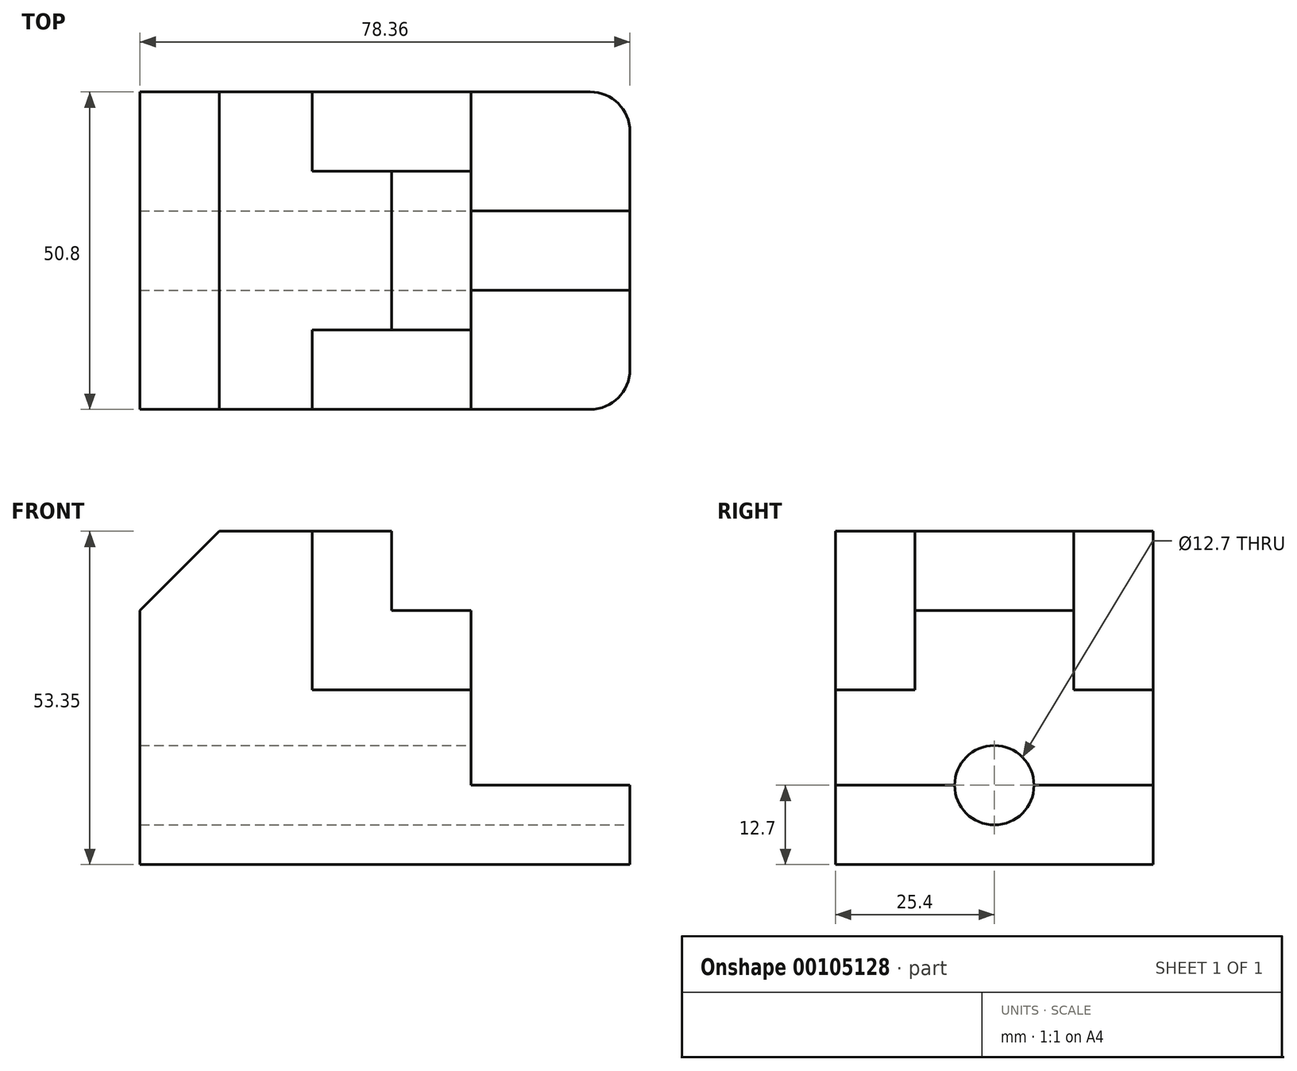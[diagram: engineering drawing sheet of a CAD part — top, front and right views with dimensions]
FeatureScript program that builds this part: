
annotation { "Feature Type Name" : "Feature", "Feature Type Description" : "" }
export const myFeature = defineFeature(function(context is Context, id is Id, definition is map)
    precondition{}
    {
        {
            var Q0;
            Q0=qCreatedBy(makeId("Front.planeOp"),FACE);
            var sketch = newSketch(context, id + "F0", { "sketchPlane" : qUnion([Q0])});
            skLineSegment(sketch, "E0", {"start": v(0, 0) * mm, "end": v(0, 53.35) * mm});
            skLineSegment(sketch, "E1", {"start": v(0, 53.35) * mm, "end": v(78.36, 53.35) * mm});
            skLineSegment(sketch, "E2", {"start": v(78.36, 53.35) * mm, "end": v(78.36, 0) * mm});
            skLineSegment(sketch, "E3", {"start": v(78.36, 0) * mm, "end": v(0, 0) * mm});
            skSolve(sketch);
        }
        {
            var Q0;
            Q0 = qSketchRegion(id + "F0", true);
            extrude(context, id + "F1", {"entities" : qUnion([Q0]), "oppositeDirection" : true, "depth" : 50.8 * mm});
        }
        {
            var Q0;
            Q0=makeQuery(id+"F1.opExtrude","CAP_FACE",FACE,{"disambiguationData":[OSD([sQuery(id+"F0.wireOp",EDGE,"E0"),sQuery(id+"F0.wireOp",EDGE,"E1"),sQuery(id+"F0.wireOp",EDGE,"E2"),sQuery(id+"F0.wireOp",EDGE,"E3")])],"isStart":true});
            var sketch = newSketch(context, id + "F2", { "sketchPlane" : qUnion([Q0])});
            skLineSegment(sketch, "E4", {"start": v(0, 40.65) * mm, "end": v(12.7, 53.35) * mm});
            skSolve(sketch);
        }
        {
            var Q0;
            {var subQ0=sQuery(id+"F2.wireOp",EDGE,"E4");Q0=makeQuery(id+"F2.imprint","IMPRINT",FACE,{"disambiguationData":[TD([[makeQuery(id+"F2.imprint","IMPRINT",EDGE,{"derivedFrom":subQ0}),1.0]])]});}
            extrude(context, id + "F3", {"entities" : qUnion([Q0]), "operationType" : NewBodyOperationType.REMOVE, "endBound" : BoundingType.THROUGH_ALL, "oppositeDirection" : true, "depth" : 25.4 * mm});
        }
        {
            var Q0;
            Q0=makeQuery(id+"F1.opExtrude","CAP_FACE",FACE,{"disambiguationData":[OSD([sQuery(id+"F0.wireOp",EDGE,"E0"),sQuery(id+"F0.wireOp",EDGE,"E1"),sQuery(id+"F0.wireOp",EDGE,"E2"),sQuery(id+"F0.wireOp",EDGE,"E3")])],"isStart":true});
            var sketch = newSketch(context, id + "F4", { "sketchPlane" : qUnion([Q0])});
            skLineSegment(sketch, "E5", {"start": v(78.36, 12.7) * mm, "end": v(52.96, 12.7) * mm});
            skLineSegment(sketch, "E6", {"start": v(52.96, 12.7) * mm, "end": v(52.96, 53.35) * mm});
            skSolve(sketch);
        }
        {
            var Q0;
            {var subQ0=sQuery(id+"F4.wireOp",EDGE,"E5");Q0=makeQuery(id+"F4.imprint","IMPRINT",FACE,{"disambiguationData":[TD([[makeQuery(id+"F4.imprint","IMPRINT",EDGE,{"derivedFrom":subQ0}),-1.0]])]});}
            extrude(context, id + "F5", {"entities" : qUnion([Q0]), "operationType" : NewBodyOperationType.REMOVE, "endBound" : BoundingType.THROUGH_ALL, "oppositeDirection" : true, "depth" : 25.4 * mm});
        }
        {
            var Q0;
            Q0=makeQuery(id+"F1.opExtrude","CAP_FACE",FACE,{"disambiguationData":[OSD([sQuery(id+"F0.wireOp",EDGE,"E0"),sQuery(id+"F0.wireOp",EDGE,"E1"),sQuery(id+"F0.wireOp",EDGE,"E2"),sQuery(id+"F0.wireOp",EDGE,"E3")])],"isStart":true});
            var sketch = newSketch(context, id + "F6", { "sketchPlane" : qUnion([Q0])});
            skLineSegment(sketch, "E7", {"start": v(40.26, 53.35) * mm, "end": v(40.26, 40.65) * mm});
            skLineSegment(sketch, "E8", {"start": v(40.26, 40.65) * mm, "end": v(52.96, 40.65) * mm});
            skSolve(sketch);
        }
        {
            var Q0;
            {var subQ0=sQuery(id+"F6.wireOp",EDGE,"E7");Q0=makeQuery(id+"F6.imprint","IMPRINT",FACE,{"disambiguationData":[TD([[makeQuery(id+"F6.imprint","IMPRINT",EDGE,{"derivedFrom":subQ0}),1.0]])]});}
            extrude(context, id + "F7", {"entities" : qUnion([Q0]), "operationType" : NewBodyOperationType.REMOVE, "endBound" : BoundingType.THROUGH_ALL, "oppositeDirection" : true, "depth" : 25.4 * mm});
        }
        {
            var Q0;
            Q0=makeQuery(id+"F1.opExtrude","CAP_FACE",FACE,{"disambiguationData":[OSD([sQuery(id+"F0.wireOp",EDGE,"E0"),sQuery(id+"F0.wireOp",EDGE,"E1"),sQuery(id+"F0.wireOp",EDGE,"E2"),sQuery(id+"F0.wireOp",EDGE,"E3")])],"isStart":true});
            var sketch = newSketch(context, id + "F8", { "sketchPlane" : qUnion([Q0])});
            skLineSegment(sketch, "E9", {"start": v(52.96, 27.95) * mm, "end": v(27.56, 27.95) * mm});
            skLineSegment(sketch, "E10", {"start": v(27.56, 27.95) * mm, "end": v(27.56, 53.35) * mm});
            skSolve(sketch);
        }
        {
            var Q0;
            {var subQ4=sQuery(id+"F8.wireOp",EDGE,"E9");Q0=makeQuery(id+"F8.imprint","IMPRINT",FACE,{"disambiguationData":[TD([[makeQuery(id+"F8.imprint","IMPRINT",EDGE,{"derivedFrom":subQ4}),-1.0]])]});}
            extrude(context, id + "F9", {"entities" : qUnion([Q0]), "operationType" : NewBodyOperationType.REMOVE, "oppositeDirection" : true, "depth" : 12.7 * mm});
        }
        {
            var Q0;
            Q0=makeQuery(id+"F1.opExtrude","CAP_FACE",FACE,{"disambiguationData":[OSD([sQuery(id+"F0.wireOp",EDGE,"E0"),sQuery(id+"F0.wireOp",EDGE,"E1"),sQuery(id+"F0.wireOp",EDGE,"E2"),sQuery(id+"F0.wireOp",EDGE,"E3")])],"isStart":false});
            var sketch = newSketch(context, id + "F10", { "sketchPlane" : qUnion([Q0])});
            skLineSegment(sketch, "E11", {"start": v(-52.96, 27.95) * mm, "end": v(-27.56, 27.95) * mm});
            skLineSegment(sketch, "E12", {"start": v(-27.56, 27.95) * mm, "end": v(-27.56, 53.35) * mm});
            skSolve(sketch);
        }
        {
            var Q0;
            {var subQ7=sQuery(id+"F10.wireOp",EDGE,"E11");Q0=makeQuery(id+"F10.imprint","IMPRINT",FACE,{"disambiguationData":[TD([[makeQuery(id+"F10.imprint","IMPRINT",EDGE,{"derivedFrom":subQ7}),1.0]])]});}
            extrude(context, id + "F11", {"entities" : qUnion([Q0]), "operationType" : NewBodyOperationType.REMOVE, "oppositeDirection" : true, "depth" : 12.7 * mm});
        }
        {
            var Q0;
            Q0=makeQuery(id+"F1.opExtrude","SWEPT_FACE",FACE,{"disambiguationData":[OSD([sQuery(id+"F0.wireOp",EDGE,"E2")])]});
            var sketch = newSketch(context, id + "F12", { "sketchPlane" : qUnion([Q0])});
            skCircle(sketch, "E13", {"center": v(25.4, 12.7) * mm, "radius": 6.35 * mm});
            skSolve(sketch);
        }
        {
            var Q0;
            {var subQ0=sQuery(id+"F12.wireOp",EDGE,"E13");var subQ1=makeQuery(id+"F5.boolean.opBoolean","COPY",EDGE,{"derivedFrom":makeQuery(id+"F5.opExtrude","SWEPT_EDGE",EDGE,{"disambiguationData":[OSD([sQuery(id+"F0.wireOp",EDGE,"E2"),sQuery(id+"F4.wireOp",EDGE,"E5")])]})});var subQ2=makeQuery(id+"F12.imprint","INTERSECT",VERTEX,{"disambiguationData":[OD(0.0)],"derivedFrom":[subQ1,subQ0]});Q0=makeQuery(id+"F12.imprint","IMPRINT",FACE,{"disambiguationData":[TD([[makeQuery(id+"F12.imprint","IMPRINT",EDGE,{"disambiguationData":[TD([[subQ2,1.0]])],"derivedFrom":subQ0}),1.0]])]});}
            var Q1;
            {var subQ0=sQuery(id+"F12.wireOp",EDGE,"E13");var subQ1=makeQuery(id+"F5.boolean.opBoolean","COPY",EDGE,{"derivedFrom":makeQuery(id+"F5.opExtrude","SWEPT_EDGE",EDGE,{"disambiguationData":[OSD([sQuery(id+"F0.wireOp",EDGE,"E2"),sQuery(id+"F4.wireOp",EDGE,"E5")])]})});var subQ2=makeQuery(id+"F12.imprint","INTERSECT",VERTEX,{"disambiguationData":[OD(0.0)],"derivedFrom":[subQ1,subQ0]});Q1=makeQuery(id+"F12.imprint","IMPRINT",FACE,{"disambiguationData":[TD([[makeQuery(id+"F12.imprint","IMPRINT",EDGE,{"disambiguationData":[TD([[subQ2,-1.0]])],"derivedFrom":subQ0}),1.0]])]});}
            var Q2;
            Q2=sQuery(id+"F12.wireOp",EDGE,"E13");
            extrude(context, id + "F13", {"entities" : qUnion([Q0, Q1]), "operationType" : NewBodyOperationType.REMOVE, "surfaceEntities" : qUnion([Q2]), "endBound" : BoundingType.THROUGH_ALL, "oppositeDirection" : true, "depth" : 25.4 * mm});
        }
        {
            var Q0;
            Q0=makeQuery(id+"F1.opExtrude","CAP_EDGE",EDGE,{"disambiguationData":[OSD([sQuery(id+"F0.wireOp",EDGE,"E2")])],"isStart":false});
            var Q1;
            Q1=makeQuery(id+"F1.opExtrude","CAP_EDGE",EDGE,{"disambiguationData":[OSD([sQuery(id+"F0.wireOp",EDGE,"E2")])],"isStart":true});
            fillet(context, id + "F14", {"entities" : qUnion([Q0, Q1]), "radius" : 6.35 * mm, "tangentPropagation" : true, "allowEdgeOverflow" : false});
        }
    });
